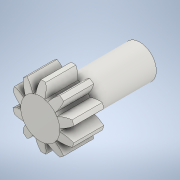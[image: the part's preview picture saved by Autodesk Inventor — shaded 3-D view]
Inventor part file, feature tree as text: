
AUTODESK INVENTOR PART (.ipt)
format: ipt  version: 2022 (Build 260153000, 153)  size: 510,464 bytes
history: native  units: mm (DEFAULTED — no unit token found)
features: sketch x6, extrude x4, plane x3, other x3, projected_geometry x2, revolve x1
ambient origin geometry x8: Origin, YZ Plane, XZ Plane, XY Plane, X Axis, Y Axis, Z Axis, Center Point
bodies: Solid1 (feature_tree)
feature tree (19):
  extrude  "Extrusion1"  Depth=6.35mm TaperAngle=0.0deg
  plane  "Work Plane1"
  plane  "Work Plane2"
  plane  "Work Plane3"
  other  "Spur Gear"
  extrude  "Extrusion2"  Depth=10.0mm TaperAngle=0.0deg
  extrude  "Extrusion3"  TaperAngle=0.0deg  [1 undecoded]
  revolve  "Revolution1"  [1 undecoded]
  extrude  "Extrusion4"  Depth=3.325mm
  sketch  "Sketch1"  dims[d0=11.961521mm d1=6.35mm d2=0.0mm]
  sketch  "Sketch2"  dims[d3=10.0mm d4=76.2mm d5=0.0mm]
  other  "Srf1"
  sketch  "Sketch3"  dims[d6=0.0mm d7=3.141593mm d9=0.0mm]
  sketch  "Sketch4"  dims[d14=0.0mm d15=23.753344mm d16=0.0mm]
  projected_geometry  "Projected Loop1"
  sketch  "Sketch5"  dims[d17=0.0mm d18=0.0mm d19=23.753344mm d20=3.325mm]
  sketch  "Sketch6"  dims[d22=0.0mm d23=0.0mm d24=6.35mm d25=12.7mm d26=0.0mm d27=15.0deg d28=90.0deg d29=2.0mm d30=0.0mm]
  projected_geometry  "Projected Loop2"
  other  "Pitch Diameter"
note: 2 required parameter values undecoded (feature->parameter linkage not recoverable at this tier; creation-order binding heuristic only, values carry confidence <= 0.55)